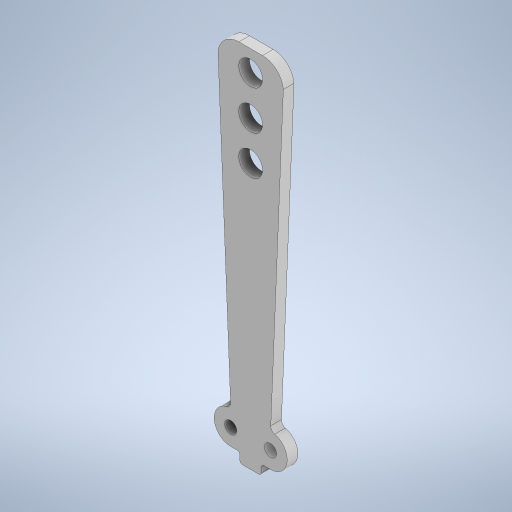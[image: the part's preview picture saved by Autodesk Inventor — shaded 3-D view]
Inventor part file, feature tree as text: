
AUTODESK INVENTOR PART (.ipt)
format: ipt  version: 2023.5 (Build 275446000, 446)  size: 307,200 bytes
history: native  units: mm
features: extrude x2, sketch x2, fillet x1, projected_geometry x1
ambient origin geometry x8: Origin, YZ Plane, XZ Plane, XY Plane, X Axis, Y Axis, Z Axis, Center Point
bodies: Solid1 (feature_tree)
feature tree (6):
  extrude  "Extrusion1"  Depth=24.987954mm
  fillet  "Fillet1"  Radius=0.841608mm
  extrude  "Extrusion2"  Depth=2.0mm
  sketch  "Sketch1"  dims[d2=15.239999mm d15=4.572mm d16=24.987954mm d17=0.841608mm]
  sketch  "Sketch2"  dims[d74=10.160001mm d75=3.948149mm d102=4.077mm d103=0.0mm d104=8.0mm d114=15.0mm d115=15.0mm d118=23.0mm d119=38.0mm d120=0.0mm d121=0.0mm d122=2.0mm d105=0.0mm d106=0.0mm d107=0.0mm d123=0.0mm d124=0.0mm d125=0.0mm]
  projected_geometry  "Projected Loop1"
